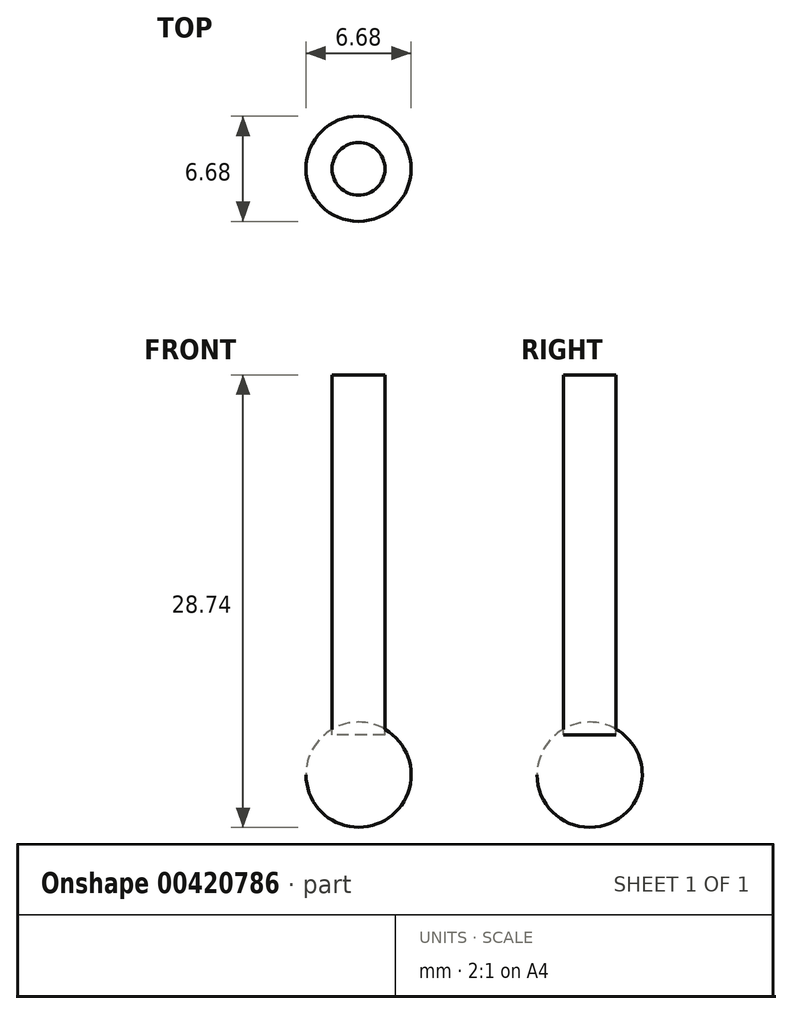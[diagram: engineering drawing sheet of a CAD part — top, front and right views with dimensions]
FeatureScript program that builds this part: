
annotation { "Feature Type Name" : "Feature", "Feature Type Description" : "" }
export const myFeature = defineFeature(function(context is Context, id is Id, definition is map)
    precondition{}
    {
        {
            var Q0;
            Q0=qCreatedBy(makeId("Top.planeOp"),FACE);
            var sketch = newSketch(context, id + "F0", { "sketchPlane" : qUnion([Q0])});
            skCircle(sketch, "E0", {"center": v(0, 0) * mm, "radius": 1.68 * mm});
            skSolve(sketch);
        }
        {
            var Q0;
            Q0=qCreatedBy(makeId("Top.planeOp"),FACE);
            cPlane(context, id + "F1", {"entities" : qUnion([Q0]), "cplaneType" : CPlaneType.OFFSET, "offset" : 22.86 * mm, "oppositeDirection" : true, "width" : 152.4 * mm, "height" : 152.4 * mm});
        }
        {
            var Q0;
            Q0=qCreatedBy(id+"F1.planeOp",FACE);
            var sketch = newSketch(context, id + "F2", { "sketchPlane" : qUnion([Q0])});
            skCircle(sketch, "E1", {"center": v(0, 0) * mm, "radius": 1.68 * mm});
            skSolve(sketch);
        }
        {
            var Q0;
            Q0=qCreatedBy(id+"F1.planeOp",FACE);
            cPlane(context, id + "F3", {"entities" : qUnion([Q0]), "cplaneType" : CPlaneType.OFFSET, "offset" : 2.54 * mm, "oppositeDirection" : true, "width" : 152.4 * mm, "height" : 152.4 * mm});
        }
        {
            var Q0;
            Q0 = qSketchRegion(id + "F0", true);
            var Q1;
            Q1 = qSketchRegion(id + "F2", true);
            loft(context, id + "F4", {"sheetProfilesArray" : [{ "sheetProfileEntities" : qUnion([Q0]) }, { "sheetProfileEntities" : qUnion([Q1]) }]});
        }
        {
            var Q0;
            Q0=qCreatedBy(id+"F3.planeOp",FACE);
            var sketch = newSketch(context, id + "F5", { "sketchPlane" : qUnion([Q0])});
            skArc(sketch, "E2", {"start": v(0, -3.34) * mm, "mid": v(3.34, 0) * mm, "end": v(0, 3.34) * mm});
            skLineSegment(sketch, "E3", {"start": v(0, 0) * mm, "end": v(0, 3.34) * mm});
            skLineSegment(sketch, "E4", {"start": v(0, 0) * mm, "end": v(0, -3.34) * mm});
            skSolve(sketch);
        }
        {
            var Q0;
            Q0 = qSketchRegion(id + "F5", true);
            var Q1;
            Q1=sQuery(id+"F5.wireOp",EDGE,"E3");
            revolve(context, id + "F6", {"entities" : qUnion([Q0]), "axis" : qUnion([Q1]), "revolveType" : RevolveType.FULL});
        }
    });
